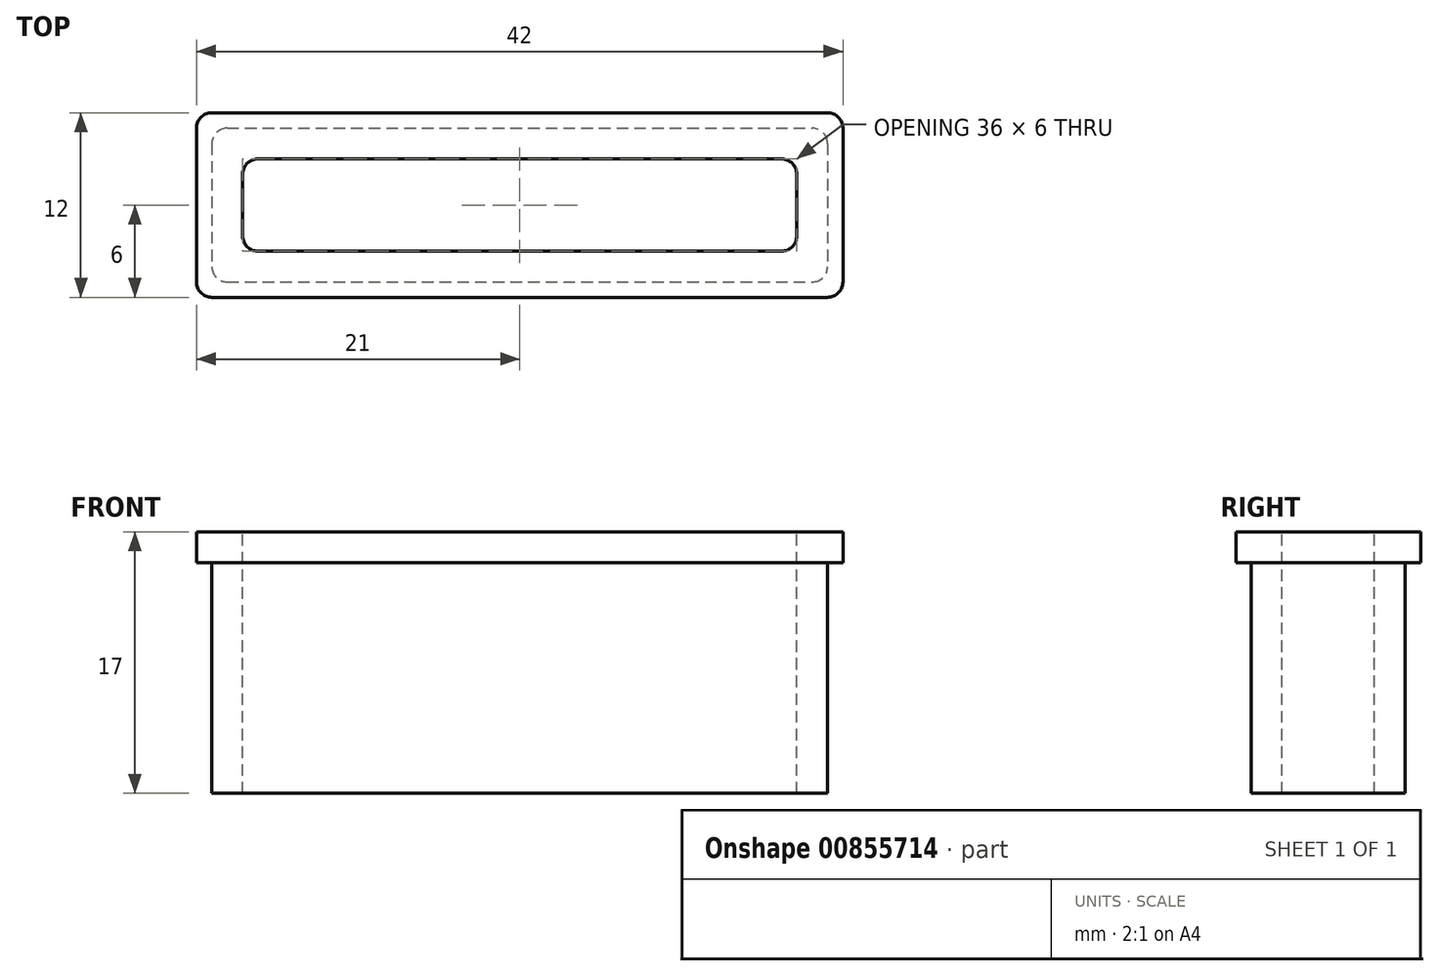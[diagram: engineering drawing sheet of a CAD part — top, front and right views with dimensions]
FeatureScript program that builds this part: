
annotation { "Feature Type Name" : "Feature", "Feature Type Description" : "" }
export const myFeature = defineFeature(function(context is Context, id is Id, definition is map)
    precondition{}
    {
        {
            var Q0;
            Q0=qCreatedBy(makeId("Top.planeOp"),FACE);
            var sketch = newSketch(context, id + "F0", { "sketchPlane" : qUnion([Q0])});
            skLineSegment(sketch, "E0.bottom", {"start": v(-20, 5) * mm, "end": v(20, 5) * mm});
            skLineSegment(sketch, "E0.top", {"start": v(-20, -5) * mm, "end": v(20, -5) * mm});
            skLineSegment(sketch, "E0.left", {"start": v(-20, 5) * mm, "end": v(-20, -5) * mm});
            skLineSegment(sketch, "E0.right", {"start": v(20, 5) * mm, "end": v(20, -5) * mm});
            skPoint(sketch, "E0.middle", {"position": v(0, 0) * mm});
            skLineSegment(sketch, "E1.bottom", {"start": v(-18, 3) * mm, "end": v(18, 3) * mm});
            skLineSegment(sketch, "E1.top", {"start": v(-18, -3) * mm, "end": v(18, -3) * mm});
            skLineSegment(sketch, "E1.left", {"start": v(-18, 3) * mm, "end": v(-18, -3) * mm});
            skLineSegment(sketch, "E1.right", {"start": v(18, 3) * mm, "end": v(18, -3) * mm});
            skSolve(sketch);
        }
        {
            var Q0;
            Q0=makeQuery(id+"F0.imprint","IMPRINT",FACE,{"disambiguationData":[TD([[makeQuery(id+"F0.imprint","IMPRINT",EDGE,{"derivedFrom":sQuery(id+"F0.wireOp",EDGE,"E0.bottom")}),-1.0]])]});
            extrude(context, id + "F1", {"entities" : qUnion([Q0]), "oppositeDirection" : true, "depth" : 15 * mm, "offsetDistance" : 25.4 * mm});
        }
        {
            var Q0;
            Q0=makeQuery(id+"F1.opExtrude","CAP_FACE",FACE,{"disambiguationData":[OSD([sQuery(id+"F0.wireOp",EDGE,"E0.bottom"),sQuery(id+"F0.wireOp",EDGE,"E0.top"),sQuery(id+"F0.wireOp",EDGE,"E0.left"),sQuery(id+"F0.wireOp",EDGE,"E0.right"),sQuery(id+"F0.wireOp",EDGE,"E1.bottom"),sQuery(id+"F0.wireOp",EDGE,"E1.top"),sQuery(id+"F0.wireOp",EDGE,"E1.left"),sQuery(id+"F0.wireOp",EDGE,"E1.right")])],"isStart":true});
            var sketch = newSketch(context, id + "F2", { "sketchPlane" : qUnion([Q0])});
            skLineSegment(sketch, "E2.bottom", {"start": v(18, -3) * mm, "end": v(-18, -3) * mm});
            skLineSegment(sketch, "E2.top", {"start": v(18, 3) * mm, "end": v(-18, 3) * mm});
            skLineSegment(sketch, "E2.left", {"start": v(18, -3) * mm, "end": v(18, 3) * mm});
            skLineSegment(sketch, "E2.right", {"start": v(-18, -3) * mm, "end": v(-18, 3) * mm});
            skPoint(sketch, "E2.middle", {"position": v(0, 0) * mm});
            skLineSegment(sketch, "E3.bottom", {"start": v(21, -6) * mm, "end": v(-21, -6) * mm});
            skLineSegment(sketch, "E3.top", {"start": v(21, 6) * mm, "end": v(-21, 6) * mm});
            skLineSegment(sketch, "E3.left", {"start": v(21, -6) * mm, "end": v(21, 6) * mm});
            skLineSegment(sketch, "E3.right", {"start": v(-21, -6) * mm, "end": v(-21, 6) * mm});
            skSolve(sketch);
        }
        {
            var Q0;
            Q0=makeQuery(id+"F2.imprint","IMPRINT",FACE,{"disambiguationData":[TD([[makeQuery(id+"F2.imprint","IMPRINT",EDGE,{"derivedFrom":sQuery(id+"F2.wireOp",EDGE,"E3.bottom")}),-1.0]])]});
            var Q1;
            Q1=makeQuery(id+"F2.imprint","IMPRINT",FACE,{"disambiguationData":[TD([[makeQuery(id+"F2.imprint","IMPRINT",EDGE,{"derivedFrom":sQuery(id+"F2.wireOp",EDGE,"E2.bottom")}),-1.0]])]});
            extrude(context, id + "F3", {"entities" : qUnion([Q0, Q1]), "operationType" : NewBodyOperationType.ADD, "depth" : 2 * mm, "offsetDistance" : 25.4 * mm});
        }
        {
            var Q0;
            Q0=makeQuery(id+"F3.opExtrude","SWEPT_EDGE",EDGE,{"disambiguationData":[OSD([sQuery(id+"F2.wireOp",EDGE,"E3.top"),sQuery(id+"F2.wireOp",EDGE,"E3.left")])]});
            var Q1;
            Q1=makeQuery(id+"F3.opExtrude","SWEPT_EDGE",EDGE,{"disambiguationData":[OSD([sQuery(id+"F2.wireOp",EDGE,"E3.bottom"),sQuery(id+"F2.wireOp",EDGE,"E3.left")])]});
            var Q2;
            Q2=makeQuery(id+"F3.opExtrude","SWEPT_EDGE",EDGE,{"disambiguationData":[OSD([sQuery(id+"F2.wireOp",EDGE,"E3.top"),sQuery(id+"F2.wireOp",EDGE,"E3.right")])]});
            var Q3;
            Q3=makeQuery(id+"F3.opExtrude","SWEPT_EDGE",EDGE,{"disambiguationData":[OSD([sQuery(id+"F2.wireOp",EDGE,"E3.bottom"),sQuery(id+"F2.wireOp",EDGE,"E3.right")])]});
            var Q4;
            Q4=makeQuery(id+"F1.opExtrude","SWEPT_EDGE",EDGE,{"disambiguationData":[OSD([sQuery(id+"F0.wireOp",EDGE,"E0.bottom"),sQuery(id+"F0.wireOp",EDGE,"E0.right")])]});
            var Q5;
            Q5=makeQuery(id+"F1.opExtrude","SWEPT_EDGE",EDGE,{"disambiguationData":[OSD([sQuery(id+"F0.wireOp",EDGE,"E0.top"),sQuery(id+"F0.wireOp",EDGE,"E0.right")])]});
            var Q6;
            Q6=makeQuery(id+"F1.opExtrude","SWEPT_EDGE",EDGE,{"disambiguationData":[OSD([sQuery(id+"F0.wireOp",EDGE,"E0.top"),sQuery(id+"F0.wireOp",EDGE,"E0.left")])]});
            var Q7;
            Q7=makeQuery(id+"F1.opExtrude","SWEPT_EDGE",EDGE,{"disambiguationData":[OSD([sQuery(id+"F0.wireOp",EDGE,"E0.bottom"),sQuery(id+"F0.wireOp",EDGE,"E0.left")])]});
            var Q8;
            Q8=makeQuery(id+"F3.boolean.opBoolean","MERGE",EDGE,{"derivedFrom":[makeQuery(id+"F1.opExtrude","SWEPT_EDGE",EDGE,{"disambiguationData":[OSD([sQuery(id+"F0.wireOp",EDGE,"E1.bottom"),sQuery(id+"F0.wireOp",EDGE,"E1.right")])]}),makeQuery(id+"F3.opExtrude","SWEPT_EDGE",EDGE,{"disambiguationData":[OSD([sQuery(id+"F2.wireOp",EDGE,"E2.top"),sQuery(id+"F2.wireOp",EDGE,"E2.left")])]})]});
            var Q9;
            Q9=makeQuery(id+"F3.boolean.opBoolean","MERGE",EDGE,{"derivedFrom":[makeQuery(id+"F1.opExtrude","SWEPT_EDGE",EDGE,{"disambiguationData":[OSD([sQuery(id+"F0.wireOp",EDGE,"E1.bottom"),sQuery(id+"F0.wireOp",EDGE,"E1.left")])]}),makeQuery(id+"F3.opExtrude","SWEPT_EDGE",EDGE,{"disambiguationData":[OSD([sQuery(id+"F2.wireOp",EDGE,"E2.top"),sQuery(id+"F2.wireOp",EDGE,"E2.right")])]})]});
            var Q10;
            Q10=makeQuery(id+"F3.boolean.opBoolean","MERGE",EDGE,{"derivedFrom":[makeQuery(id+"F1.opExtrude","SWEPT_EDGE",EDGE,{"disambiguationData":[OSD([sQuery(id+"F0.wireOp",EDGE,"E1.top"),sQuery(id+"F0.wireOp",EDGE,"E1.left")])]}),makeQuery(id+"F3.opExtrude","SWEPT_EDGE",EDGE,{"disambiguationData":[OSD([sQuery(id+"F2.wireOp",EDGE,"E2.bottom"),sQuery(id+"F2.wireOp",EDGE,"E2.right")])]})]});
            var Q11;
            Q11=makeQuery(id+"F3.boolean.opBoolean","MERGE",EDGE,{"derivedFrom":[makeQuery(id+"F1.opExtrude","SWEPT_EDGE",EDGE,{"disambiguationData":[OSD([sQuery(id+"F0.wireOp",EDGE,"E1.top"),sQuery(id+"F0.wireOp",EDGE,"E1.right")])]}),makeQuery(id+"F3.opExtrude","SWEPT_EDGE",EDGE,{"disambiguationData":[OSD([sQuery(id+"F2.wireOp",EDGE,"E2.bottom"),sQuery(id+"F2.wireOp",EDGE,"E2.left")])]})]});
            fillet(context, id + "F4", {"entities" : qUnion([Q0, Q1, Q2, Q3, Q4, Q5, Q6, Q7, Q8, Q9, Q10, Q11]), "radius" : 1 * mm, "tangentPropagation" : true, "allowEdgeOverflow" : false});
        }
    });
